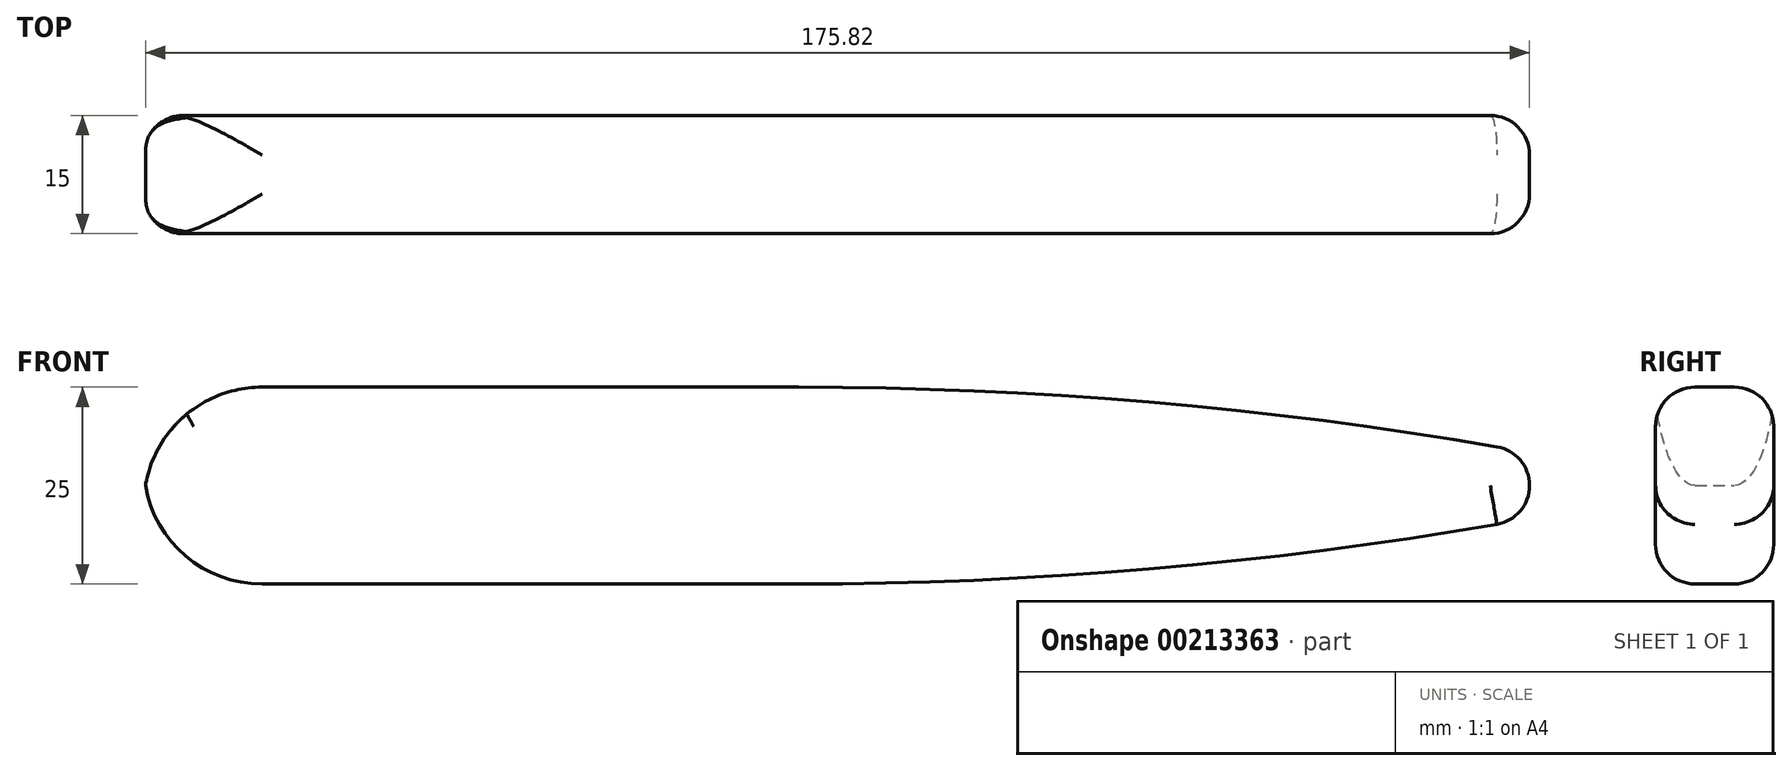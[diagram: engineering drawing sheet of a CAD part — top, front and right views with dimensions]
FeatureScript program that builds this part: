
annotation { "Feature Type Name" : "Feature", "Feature Type Description" : "" }
export const myFeature = defineFeature(function(context is Context, id is Id, definition is map)
    precondition{}
    {
        {
            var Q0;
            Q0=qCreatedBy(makeId("Top.planeOp"),FACE);
            var sketch = newSketch(context, id + "F0", { "sketchPlane" : qUnion([Q0])});
            skLineSegment(sketch, "E0.bottom", {"start": v(-90.3, 42.1) * mm, "end": v(89.7, 42.1) * mm});
            skLineSegment(sketch, "E0.top", {"start": v(-90.3, 27.1) * mm, "end": v(89.7, 27.1) * mm});
            skLineSegment(sketch, "E0.left", {"start": v(-90.3, 42.1) * mm, "end": v(-90.3, 27.1) * mm});
            skLineSegment(sketch, "E0.right", {"start": v(89.7, 42.1) * mm, "end": v(89.7, 27.1) * mm});
            skSolve(sketch);
        }
        {
            var Q0;
            Q0 = qSketchRegion(id + "F0", true);
            extrude(context, id + "F1", {"entities" : qUnion([Q0]), "depth" : 25 * mm});
        }
        {
            var Q0;
            Q0=makeQuery(id+"F1.opExtrude","CAP_EDGE",EDGE,{"disambiguationData":[OSD([sQuery(id+"F0.wireOp",EDGE,"E0.right")])],"isStart":false});
            var Q1;
            Q1=makeQuery(id+"F1.opExtrude","CAP_EDGE",EDGE,{"disambiguationData":[OSD([sQuery(id+"F0.wireOp",EDGE,"E0.right")])],"isStart":true});
            chamfer(context, id + "F2", {"entities" : qUnion([Q0, Q1]), "chamferType" : ChamferType.OFFSET_ANGLE, "width" : 9 * mm, "oppositeDirection" : false, "angle" : 80 * degree, "tangentPropagation" : true});
        }
        {
            var Q0;
            {var subQ0=sQuery(id+"F0.wireOp",EDGE,"E0.right");Q0=makeQuery(id+"F2.opChamfer","BLEND_EDGE",EDGE,{"blendedFrom":[makeQuery(id+"F1.opExtrude","CAP_EDGE",EDGE,{"disambiguationData":[OSD([subQ0])],"isStart":true}),makeQuery(id+"F1.opExtrude","SWEPT_FACE",FACE,{"disambiguationData":[OSD([subQ0])]})],"blendedInto":[makeQuery(id+"F1.opExtrude","SWEPT_FACE",FACE,{"disambiguationData":[OSD([subQ0])]})]});}
            var Q1;
            {var subQ0=sQuery(id+"F0.wireOp",EDGE,"E0.right");Q1=makeQuery(id+"F2.opChamfer","BLEND_EDGE",EDGE,{"blendedFrom":[makeQuery(id+"F1.opExtrude","CAP_EDGE",EDGE,{"disambiguationData":[OSD([subQ0])],"isStart":false}),makeQuery(id+"F1.opExtrude","SWEPT_FACE",FACE,{"disambiguationData":[OSD([subQ0])]})],"blendedInto":[makeQuery(id+"F1.opExtrude","SWEPT_FACE",FACE,{"disambiguationData":[OSD([subQ0])]})]});}
            fillet(context, id + "F3", {"entities" : qUnion([Q0, Q1]), "radius" : 5 * mm, "tangentPropagation" : true, "allowEdgeOverflow" : false});
        }
        {
            var Q0;
            {var subQ0=sQuery(id+"F0.wireOp",EDGE,"E0.right");Q0=makeQuery(id+"F2.opChamfer","BLEND_EDGE",EDGE,{"blendedFrom":[makeQuery(id+"F1.opExtrude","CAP_EDGE",EDGE,{"disambiguationData":[OSD([subQ0])],"isStart":true}),makeQuery(id+"F1.opExtrude","CAP_FACE",FACE,{"disambiguationData":[OSD([sQuery(id+"F0.wireOp",EDGE,"E0.bottom"),sQuery(id+"F0.wireOp",EDGE,"E0.top"),sQuery(id+"F0.wireOp",EDGE,"E0.left"),subQ0])],"isStart":true})],"blendedInto":[makeQuery(id+"F1.opExtrude","CAP_FACE",FACE,{"disambiguationData":[OSD([sQuery(id+"F0.wireOp",EDGE,"E0.bottom"),sQuery(id+"F0.wireOp",EDGE,"E0.top"),sQuery(id+"F0.wireOp",EDGE,"E0.left"),subQ0])],"isStart":true})]});}
            var Q1;
            {var subQ0=sQuery(id+"F0.wireOp",EDGE,"E0.right");Q1=makeQuery(id+"F2.opChamfer","BLEND_EDGE",EDGE,{"blendedFrom":[makeQuery(id+"F1.opExtrude","CAP_EDGE",EDGE,{"disambiguationData":[OSD([subQ0])],"isStart":false}),makeQuery(id+"F1.opExtrude","CAP_FACE",FACE,{"disambiguationData":[OSD([sQuery(id+"F0.wireOp",EDGE,"E0.bottom"),sQuery(id+"F0.wireOp",EDGE,"E0.top"),sQuery(id+"F0.wireOp",EDGE,"E0.left"),subQ0])],"isStart":false})],"blendedInto":[makeQuery(id+"F1.opExtrude","CAP_FACE",FACE,{"disambiguationData":[OSD([sQuery(id+"F0.wireOp",EDGE,"E0.bottom"),sQuery(id+"F0.wireOp",EDGE,"E0.top"),sQuery(id+"F0.wireOp",EDGE,"E0.left"),subQ0])],"isStart":false})]});}
            fillet(context, id + "F4", {"entities" : qUnion([Q0, Q1]), "radius" : 523.58 * mm, "tangentPropagation" : true, "allowEdgeOverflow" : false});
        }
        {
            var Q0;
            Q0=makeQuery(id+"F1.opExtrude","CAP_EDGE",EDGE,{"disambiguationData":[OSD([sQuery(id+"F0.wireOp",EDGE,"E0.left")])],"isStart":false});
            var Q1;
            Q1=makeQuery(id+"F1.opExtrude","CAP_EDGE",EDGE,{"disambiguationData":[OSD([sQuery(id+"F0.wireOp",EDGE,"E0.left")])],"isStart":true});
            fillet(context, id + "F5", {"entities" : qUnion([Q0, Q1]), "radius" : 15 * mm, "tangentPropagation" : true, "allowEdgeOverflow" : false});
        }
        {
            var Q0;
            Q0=makeQuery(id+"F1.opExtrude","CAP_EDGE",EDGE,{"disambiguationData":[OSD([sQuery(id+"F0.wireOp",EDGE,"E0.bottom")])],"isStart":true});
            var Q1;
            {var subQ0=sQuery(id+"F0.wireOp",EDGE,"E0.bottom");var subQ1=sQuery(id+"F0.wireOp",EDGE,"E0.right");Q1=makeQuery(id+"F4.opFillet","BLEND_EDGE",EDGE,{"blendedFrom":[makeQuery(id+"F2.opChamfer","BLEND_EDGE",EDGE,{"blendedFrom":[makeQuery(id+"F1.opExtrude","CAP_EDGE",EDGE,{"disambiguationData":[OSD([subQ1])],"isStart":true}),makeQuery(id+"F1.opExtrude","CAP_FACE",FACE,{"disambiguationData":[OSD([subQ0,sQuery(id+"F0.wireOp",EDGE,"E0.top"),sQuery(id+"F0.wireOp",EDGE,"E0.left"),subQ1])],"isStart":true})],"blendedInto":[makeQuery(id+"F1.opExtrude","CAP_FACE",FACE,{"disambiguationData":[OSD([subQ0,sQuery(id+"F0.wireOp",EDGE,"E0.top"),sQuery(id+"F0.wireOp",EDGE,"E0.left"),subQ1])],"isStart":true})]}),makeQuery(id+"F1.opExtrude","SWEPT_FACE",FACE,{"disambiguationData":[OSD([subQ0])]})],"blendedInto":[makeQuery(id+"F1.opExtrude","SWEPT_FACE",FACE,{"disambiguationData":[OSD([subQ0])]})]});}
            var Q2;
            {var subQ0=sQuery(id+"F0.wireOp",EDGE,"E0.top");var subQ1=sQuery(id+"F0.wireOp",EDGE,"E0.right");Q2=makeQuery(id+"F4.opFillet","BLEND_EDGE",EDGE,{"blendedFrom":[makeQuery(id+"F2.opChamfer","BLEND_EDGE",EDGE,{"blendedFrom":[makeQuery(id+"F1.opExtrude","CAP_EDGE",EDGE,{"disambiguationData":[OSD([subQ1])],"isStart":true}),makeQuery(id+"F1.opExtrude","CAP_FACE",FACE,{"disambiguationData":[OSD([sQuery(id+"F0.wireOp",EDGE,"E0.bottom"),subQ0,sQuery(id+"F0.wireOp",EDGE,"E0.left"),subQ1])],"isStart":true})],"blendedInto":[makeQuery(id+"F1.opExtrude","CAP_FACE",FACE,{"disambiguationData":[OSD([sQuery(id+"F0.wireOp",EDGE,"E0.bottom"),subQ0,sQuery(id+"F0.wireOp",EDGE,"E0.left"),subQ1])],"isStart":true})]}),makeQuery(id+"F1.opExtrude","SWEPT_FACE",FACE,{"disambiguationData":[OSD([subQ0])]})],"blendedInto":[makeQuery(id+"F1.opExtrude","SWEPT_FACE",FACE,{"disambiguationData":[OSD([subQ0])]})]});}
            var Q3;
            Q3=makeQuery(id+"F1.opExtrude","CAP_EDGE",EDGE,{"disambiguationData":[OSD([sQuery(id+"F0.wireOp",EDGE,"E0.top")])],"isStart":true});
            fillet(context, id + "F6", {"entities" : qUnion([Q0, Q1, Q2, Q3]), "radius" : 5 * mm, "tangentPropagation" : true, "allowEdgeOverflow" : false});
        }
        {
            var Q0;
            {var subQ0=sQuery(id+"F0.wireOp",EDGE,"E0.right");var subQ1=makeQuery(id+"F1.opExtrude","CAP_EDGE",EDGE,{"disambiguationData":[OSD([subQ0])],"isStart":true});Q0=makeQuery(id+"F6.opFillet","BLEND_EDGE",EDGE,{"blendedFrom":[makeQuery(id+"F2.opChamfer","BLEND_EDGE",EDGE,{"blendedFrom":[subQ1,makeQuery(id+"F1.opExtrude","SWEPT_FACE",FACE,{"disambiguationData":[OSD([sQuery(id+"F0.wireOp",EDGE,"E0.bottom")])]})],"blendedInto":[makeQuery(id+"F1.opExtrude","SWEPT_FACE",FACE,{"disambiguationData":[OSD([sQuery(id+"F0.wireOp",EDGE,"E0.bottom")])]})]}),makeQuery(id+"F3.opFillet","BLEND_FACE",FACE,{"disambiguationData":[OSD([subQ0]),TDD([makeQuery(id+"F2.opChamfer","BLEND_EDGE",EDGE,{"blendedFrom":[subQ1,makeQuery(id+"F1.opExtrude","SWEPT_FACE",FACE,{"disambiguationData":[OSD([subQ0])]})],"blendedInto":[makeQuery(id+"F1.opExtrude","SWEPT_FACE",FACE,{"disambiguationData":[OSD([subQ0])]})]})])]})],"blendedInto":[makeQuery(id+"F3.opFillet","BLEND_FACE",FACE,{"disambiguationData":[OSD([subQ0]),TDD([makeQuery(id+"F2.opChamfer","BLEND_EDGE",EDGE,{"blendedFrom":[subQ1,makeQuery(id+"F1.opExtrude","SWEPT_FACE",FACE,{"disambiguationData":[OSD([subQ0])]})],"blendedInto":[makeQuery(id+"F1.opExtrude","SWEPT_FACE",FACE,{"disambiguationData":[OSD([subQ0])]})]})])]})]});}
            var Q1;
            {var subQ0=sQuery(id+"F0.wireOp",EDGE,"E0.right");var subQ1=makeQuery(id+"F1.opExtrude","CAP_EDGE",EDGE,{"disambiguationData":[OSD([subQ0])],"isStart":true});Q1=makeQuery(id+"F6.opFillet","BLEND_EDGE",EDGE,{"blendedFrom":[makeQuery(id+"F2.opChamfer","BLEND_EDGE",EDGE,{"blendedFrom":[subQ1,makeQuery(id+"F1.opExtrude","SWEPT_FACE",FACE,{"disambiguationData":[OSD([sQuery(id+"F0.wireOp",EDGE,"E0.top")])]})],"blendedInto":[makeQuery(id+"F1.opExtrude","SWEPT_FACE",FACE,{"disambiguationData":[OSD([sQuery(id+"F0.wireOp",EDGE,"E0.top")])]})]}),makeQuery(id+"F3.opFillet","BLEND_FACE",FACE,{"disambiguationData":[OSD([subQ0]),TDD([makeQuery(id+"F2.opChamfer","BLEND_EDGE",EDGE,{"blendedFrom":[subQ1,makeQuery(id+"F1.opExtrude","SWEPT_FACE",FACE,{"disambiguationData":[OSD([subQ0])]})],"blendedInto":[makeQuery(id+"F1.opExtrude","SWEPT_FACE",FACE,{"disambiguationData":[OSD([subQ0])]})]})])]})],"blendedInto":[makeQuery(id+"F3.opFillet","BLEND_FACE",FACE,{"disambiguationData":[OSD([subQ0]),TDD([makeQuery(id+"F2.opChamfer","BLEND_EDGE",EDGE,{"blendedFrom":[subQ1,makeQuery(id+"F1.opExtrude","SWEPT_FACE",FACE,{"disambiguationData":[OSD([subQ0])]})],"blendedInto":[makeQuery(id+"F1.opExtrude","SWEPT_FACE",FACE,{"disambiguationData":[OSD([subQ0])]})]})])]})]});}
            var Q2;
            {var subQ0=sQuery(id+"F0.wireOp",EDGE,"E0.top");var subQ1=makeQuery(id+"F1.opExtrude","SWEPT_FACE",FACE,{"disambiguationData":[OSD([subQ0])]});var subQ2=sQuery(id+"F0.wireOp",EDGE,"E0.right");var subQ3=makeQuery(id+"F1.opExtrude","CAP_EDGE",EDGE,{"disambiguationData":[OSD([subQ2])],"isStart":true});Q2=makeQuery(id+"F6.opFillet","BLEND_EDGE",EDGE,{"blendedFrom":[makeQuery(id+"F4.opFillet","BLEND_EDGE",EDGE,{"blendedFrom":[makeQuery(id+"F2.opChamfer","BLEND_EDGE",EDGE,{"blendedFrom":[subQ3,makeQuery(id+"F1.opExtrude","CAP_FACE",FACE,{"disambiguationData":[OSD([sQuery(id+"F0.wireOp",EDGE,"E0.bottom"),subQ0,sQuery(id+"F0.wireOp",EDGE,"E0.left"),subQ2])],"isStart":true})],"blendedInto":[makeQuery(id+"F1.opExtrude","CAP_FACE",FACE,{"disambiguationData":[OSD([sQuery(id+"F0.wireOp",EDGE,"E0.bottom"),subQ0,sQuery(id+"F0.wireOp",EDGE,"E0.left"),subQ2])],"isStart":true})]}),subQ1],"blendedInto":[subQ1]}),makeQuery(id+"F2.opChamfer","BLEND_EDGE",EDGE,{"blendedFrom":[subQ3,subQ1],"blendedInto":[subQ1]})],"blendedInto":[]});}
            var Q3;
            {var subQ0=sQuery(id+"F0.wireOp",EDGE,"E0.bottom");var subQ1=makeQuery(id+"F1.opExtrude","SWEPT_FACE",FACE,{"disambiguationData":[OSD([subQ0])]});var subQ2=sQuery(id+"F0.wireOp",EDGE,"E0.right");var subQ3=makeQuery(id+"F1.opExtrude","CAP_EDGE",EDGE,{"disambiguationData":[OSD([subQ2])],"isStart":true});Q3=makeQuery(id+"F6.opFillet","BLEND_EDGE",EDGE,{"blendedFrom":[makeQuery(id+"F4.opFillet","BLEND_EDGE",EDGE,{"blendedFrom":[makeQuery(id+"F2.opChamfer","BLEND_EDGE",EDGE,{"blendedFrom":[subQ3,makeQuery(id+"F1.opExtrude","CAP_FACE",FACE,{"disambiguationData":[OSD([subQ0,sQuery(id+"F0.wireOp",EDGE,"E0.top"),sQuery(id+"F0.wireOp",EDGE,"E0.left"),subQ2])],"isStart":true})],"blendedInto":[makeQuery(id+"F1.opExtrude","CAP_FACE",FACE,{"disambiguationData":[OSD([subQ0,sQuery(id+"F0.wireOp",EDGE,"E0.top"),sQuery(id+"F0.wireOp",EDGE,"E0.left"),subQ2])],"isStart":true})]}),subQ1],"blendedInto":[subQ1]}),makeQuery(id+"F2.opChamfer","BLEND_EDGE",EDGE,{"blendedFrom":[subQ3,subQ1],"blendedInto":[subQ1]})],"blendedInto":[]});}
            fillet(context, id + "F7", {"entities" : qUnion([Q0, Q1, Q2, Q3]), "radius" : 1.35 * mm, "tangentPropagation" : true, "allowEdgeOverflow" : false});
        }
        {
            var Q0;
            {var subQ0=sQuery(id+"F0.wireOp",EDGE,"E0.top");var subQ1=sQuery(id+"F0.wireOp",EDGE,"E0.right");Q0=makeQuery(id+"F4.opFillet","BLEND_EDGE",EDGE,{"blendedFrom":[makeQuery(id+"F2.opChamfer","BLEND_EDGE",EDGE,{"blendedFrom":[makeQuery(id+"F1.opExtrude","CAP_EDGE",EDGE,{"disambiguationData":[OSD([subQ1])],"isStart":false}),makeQuery(id+"F1.opExtrude","CAP_FACE",FACE,{"disambiguationData":[OSD([sQuery(id+"F0.wireOp",EDGE,"E0.bottom"),subQ0,sQuery(id+"F0.wireOp",EDGE,"E0.left"),subQ1])],"isStart":false})],"blendedInto":[makeQuery(id+"F1.opExtrude","CAP_FACE",FACE,{"disambiguationData":[OSD([sQuery(id+"F0.wireOp",EDGE,"E0.bottom"),subQ0,sQuery(id+"F0.wireOp",EDGE,"E0.left"),subQ1])],"isStart":false})]}),makeQuery(id+"F1.opExtrude","SWEPT_FACE",FACE,{"disambiguationData":[OSD([subQ0])]})],"blendedInto":[makeQuery(id+"F1.opExtrude","SWEPT_FACE",FACE,{"disambiguationData":[OSD([subQ0])]})]});}
            var Q1;
            {var subQ0=sQuery(id+"F0.wireOp",EDGE,"E0.bottom");var subQ1=sQuery(id+"F0.wireOp",EDGE,"E0.right");Q1=makeQuery(id+"F4.opFillet","BLEND_EDGE",EDGE,{"blendedFrom":[makeQuery(id+"F2.opChamfer","BLEND_EDGE",EDGE,{"blendedFrom":[makeQuery(id+"F1.opExtrude","CAP_EDGE",EDGE,{"disambiguationData":[OSD([subQ1])],"isStart":false}),makeQuery(id+"F1.opExtrude","CAP_FACE",FACE,{"disambiguationData":[OSD([subQ0,sQuery(id+"F0.wireOp",EDGE,"E0.top"),sQuery(id+"F0.wireOp",EDGE,"E0.left"),subQ1])],"isStart":false})],"blendedInto":[makeQuery(id+"F1.opExtrude","CAP_FACE",FACE,{"disambiguationData":[OSD([subQ0,sQuery(id+"F0.wireOp",EDGE,"E0.top"),sQuery(id+"F0.wireOp",EDGE,"E0.left"),subQ1])],"isStart":false})]}),makeQuery(id+"F1.opExtrude","SWEPT_FACE",FACE,{"disambiguationData":[OSD([subQ0])]})],"blendedInto":[makeQuery(id+"F1.opExtrude","SWEPT_FACE",FACE,{"disambiguationData":[OSD([subQ0])]})]});}
            fillet(context, id + "F8", {"entities" : qUnion([Q0, Q1]), "radius" : 5 * mm, "tangentPropagation" : true, "allowEdgeOverflow" : false});
        }
    });
